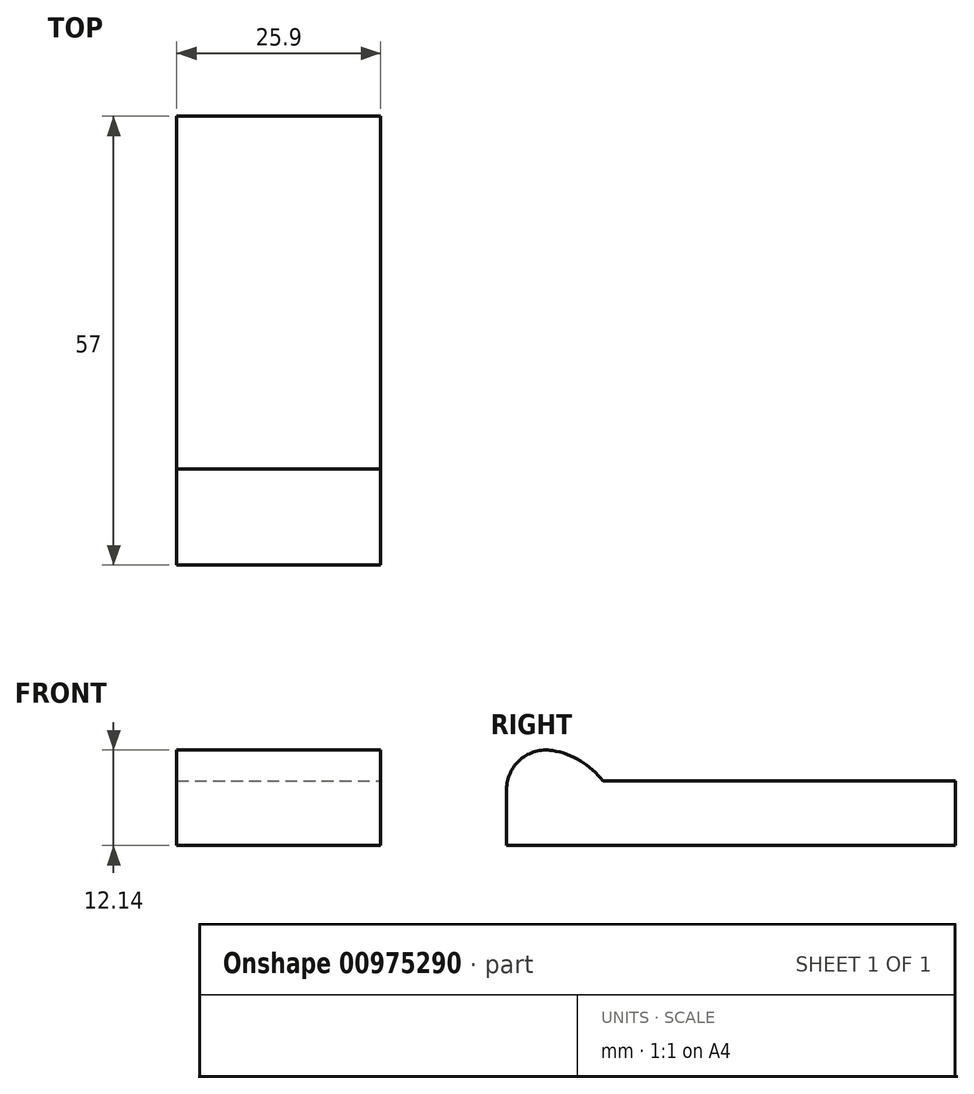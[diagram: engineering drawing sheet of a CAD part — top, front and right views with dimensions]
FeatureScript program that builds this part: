
annotation { "Feature Type Name" : "Feature", "Feature Type Description" : "" }
export const myFeature = defineFeature(function(context is Context, id is Id, definition is map)
    precondition{}
    {
        {
            var Q0;
            Q0=qCreatedBy(makeId("Top.planeOp"),FACE);
            var sketch = newSketch(context, id + "F0", { "sketchPlane" : qUnion([Q0])});
            skLineSegment(sketch, "E0.bottom", {"start": v(-4.9, 35.9) * mm, "end": v(21, 35.9) * mm});
            skLineSegment(sketch, "E0.top", {"start": v(-4.9, -21.1) * mm, "end": v(21, -21.1) * mm});
            skLineSegment(sketch, "E0.left", {"start": v(-4.9, 35.9) * mm, "end": v(-4.9, -21.1) * mm});
            skLineSegment(sketch, "E0.right", {"start": v(21, 35.9) * mm, "end": v(21, -21.1) * mm});
            skSolve(sketch);
        }
        {
            var Q0;
            Q0=makeQuery(id+"F0.imprint","IMPRINT",FACE,{"disambiguationData":[TD([[makeQuery(id+"F0.imprint","IMPRINT",EDGE,{"derivedFrom":sQuery(id+"F0.wireOp",EDGE,"E0.bottom")}),-1.0]])]});
            extrude(context, id + "F1", {"entities" : qUnion([Q0]), "depth" : 8.2 * mm, "offsetDistance" : 25 * mm});
        }
        {
            var Q0;
            Q0=makeQuery(id+"F1.opExtrude","CAP_FACE",FACE,{"disambiguationData":[OSD([sQuery(id+"F0.wireOp",EDGE,"E0.bottom"),sQuery(id+"F0.wireOp",EDGE,"E0.top"),sQuery(id+"F0.wireOp",EDGE,"E0.left"),sQuery(id+"F0.wireOp",EDGE,"E0.right")])],"isStart":false});
            var sketch = newSketch(context, id + "F2", { "sketchPlane" : qUnion([Q0])});
            skLineSegment(sketch, "E1.bottom", {"start": v(-4.9, -21.1) * mm, "end": v(21, -21.1) * mm});
            skLineSegment(sketch, "E1.top", {"start": v(-4.9, -8.9) * mm, "end": v(21, -8.9) * mm});
            skLineSegment(sketch, "E1.left", {"start": v(-4.9, -21.1) * mm, "end": v(-4.9, -8.9) * mm});
            skLineSegment(sketch, "E1.right", {"start": v(21, -21.1) * mm, "end": v(21, -8.9) * mm});
            skSolve(sketch);
        }
        {
            var Q0;
            Q0 = qSketchRegion(id + "F2", true);
            extrude(context, id + "F3", {"entities" : qUnion([Q0]), "operationType" : NewBodyOperationType.ADD, "depth" : 4 * mm, "offsetDistance" : 25 * mm});
        }
        {
            var Q0;
            Q0=makeQuery(id+"F3.opExtrude","CAP_EDGE",EDGE,{"disambiguationData":[OSD([sQuery(id+"F2.wireOp",EDGE,"E1.top")])],"isStart":false});
            fillet(context, id + "F4", {"entities" : qUnion([Q0]), "radius" : 10 * mm, "tangentPropagation" : true, "allowEdgeOverflow" : false});
        }
        {
            var Q0;
            Q0=makeQuery(id+"F3.opExtrude","CAP_EDGE",EDGE,{"disambiguationData":[OSD([sQuery(id+"F2.wireOp",EDGE,"E1.bottom")])],"isStart":false});
            fillet(context, id + "F5", {"entities" : qUnion([Q0]), "radius" : 5 * mm, "tangentPropagation" : true, "allowEdgeOverflow" : false});
        }
    });
